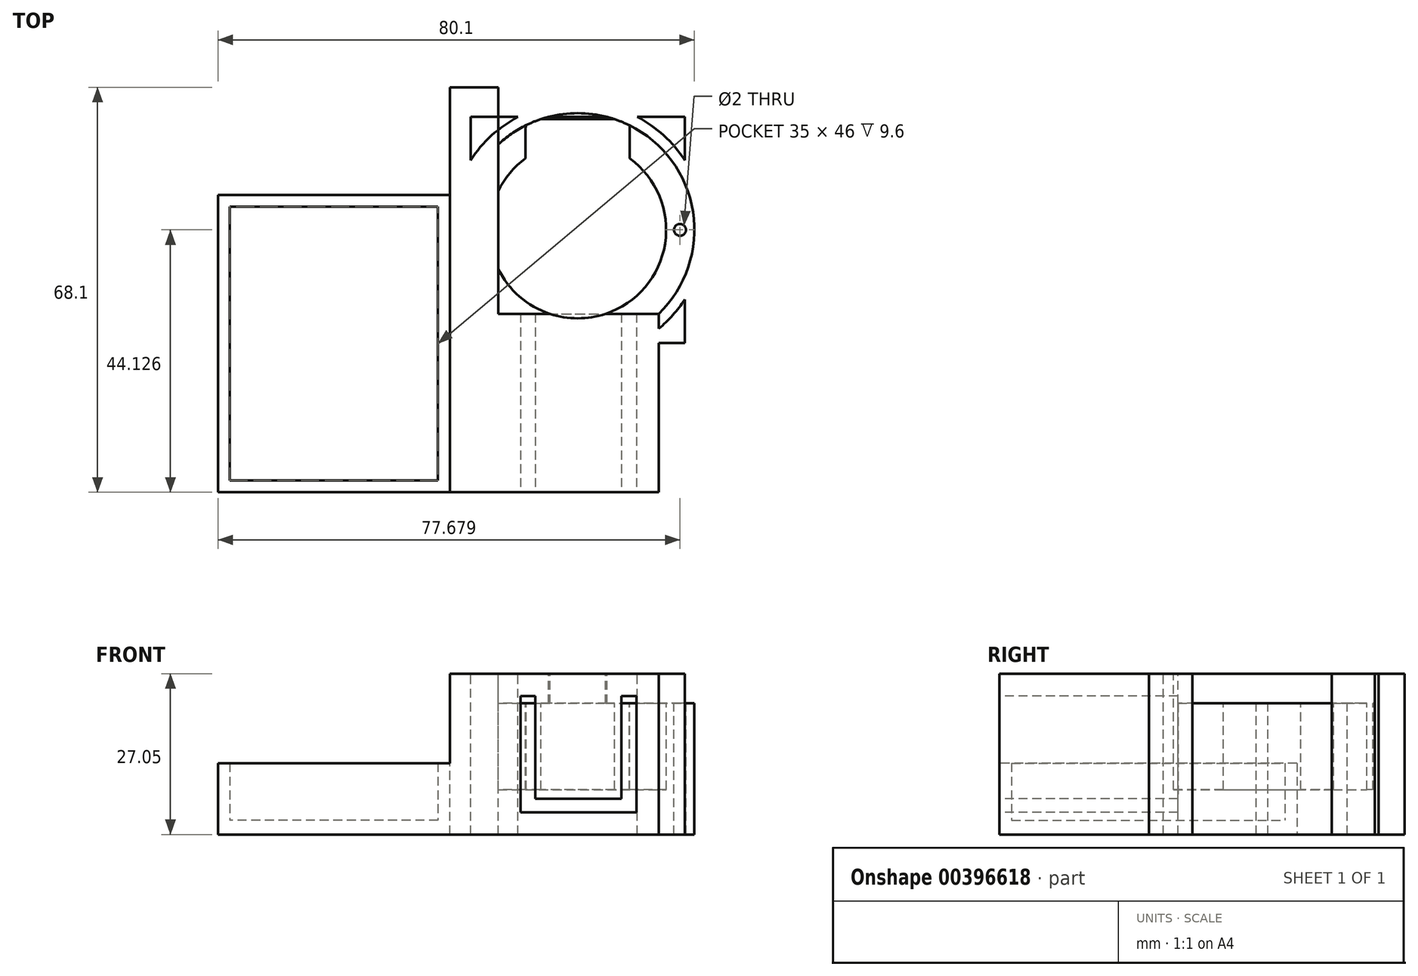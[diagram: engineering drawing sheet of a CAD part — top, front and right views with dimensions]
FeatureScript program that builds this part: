
annotation { "Feature Type Name" : "Feature", "Feature Type Description" : "" }
export const myFeature = defineFeature(function(context is Context, id is Id, definition is map)
    precondition{}
    {
        {
            var Q0;
            Q0=qCreatedBy(makeId("Front.planeOp"),FACE);
            var sketch = newSketch(context, id + "F0", { "sketchPlane" : qUnion([Q0])});
            skLineSegment(sketch, "E0", {"start": v(0, 65.65) * mm, "end": v(0, -40.44) * mm, "construction": true});
            skLineSegment(sketch, "E1", {"start": v(0, 0) * mm, "end": v(-9.75, 0) * mm});
            skLineSegment(sketch, "E2", {"start": v(-9.75, 0) * mm, "end": v(-9.75, 19.55) * mm});
            skLineSegment(sketch, "E3", {"start": v(-9.75, 19.55) * mm, "end": v(-7.25, 19.55) * mm});
            skLineSegment(sketch, "E4", {"start": v(-7.25, 19.55) * mm, "end": v(-7.25, 2.25) * mm});
            skLineSegment(sketch, "E5", {"start": v(-7.25, 2.25) * mm, "end": v(0, 2.25) * mm});
            skLineSegment(sketch, "E6.MirrorCS", {"start": v(9.75, 19.55) * mm, "end": v(7.25, 19.55) * mm});
            skLineSegment(sketch, "E7.MirrorCS", {"start": v(0, 0) * mm, "end": v(9.75, 0) * mm});
            skLineSegment(sketch, "E8.MirrorCS", {"start": v(9.75, 0) * mm, "end": v(9.75, 19.55) * mm});
            skLineSegment(sketch, "E9.MirrorCS", {"start": v(7.25, 19.55) * mm, "end": v(7.25, 2.25) * mm});
            skLineSegment(sketch, "E10.MirrorCS", {"start": v(7.25, 2.25) * mm, "end": v(0, 2.25) * mm});
            skLineSegment(sketch, "E11.0", {"start": v(-13.5, 23.3) * mm, "end": v(0, 23.3) * mm});
            skLineSegment(sketch, "E11.1", {"start": v(-13.5, -3.75) * mm, "end": v(-13.5, 23.3) * mm});
            skLineSegment(sketch, "E11.2", {"start": v(0, -3.75) * mm, "end": v(-13.5, -3.75) * mm});
            skLineSegment(sketch, "E12.MirrorCS", {"start": v(0, -3.75) * mm, "end": v(13.5, -3.75) * mm});
            skLineSegment(sketch, "E13.MirrorCS", {"start": v(13.5, 23.3) * mm, "end": v(0, 23.3) * mm});
            skLineSegment(sketch, "E14.MirrorCS", {"start": v(13.5, -3.75) * mm, "end": v(13.5, 23.3) * mm});
            skLineSegment(sketch, "E15", {"start": v(-13.5, 23.3) * mm, "end": v(-18, 23.3) * mm});
            skLineSegment(sketch, "E16", {"start": v(-18, 23.3) * mm, "end": v(-18, -3.75) * mm});
            skLineSegment(sketch, "E17", {"start": v(-18, -3.75) * mm, "end": v(-13.5, -3.75) * mm});
            skLineSegment(sketch, "E18.MirrorCS", {"start": v(18, -3.75) * mm, "end": v(13.5, -3.75) * mm});
            skLineSegment(sketch, "E19.MirrorCS", {"start": v(18, 23.3) * mm, "end": v(18, -3.75) * mm});
            skLineSegment(sketch, "E20.MirrorCS", {"start": v(13.5, 23.3) * mm, "end": v(18, 23.3) * mm});
            skSolve(sketch);
        }
        {
            var Q0;
            Q0=makeQuery(id+"F0.imprint","IMPRINT",FACE,{"disambiguationData":[TD([[makeQuery(id+"F0.imprint","IMPRINT",EDGE,{"derivedFrom":sQuery(id+"F0.wireOp",EDGE,"E1")}),1.0]])]});
            extrude(context, id + "F1", {"entities" : qUnion([Q0]), "oppositeDirection" : true, "depth" : 30 * mm});
        }
        {
            var Q0;
            {var subQ0=sQuery(id+"F0.wireOp",EDGE,"E13.MirrorCS");var subQ1=sQuery(id+"F0.wireOp",EDGE,"E11.0");Q0=makeQuery(id+"FVVeJcuvD0pZku6_1.boolean.opBoolean","MERGE",FACE,{"derivedFrom":[makeQuery(id+"F1.opExtrude","SWEPT_FACE",FACE,{"disambiguationData":[OSD([subQ1,subQ0])]}),makeQuery(id+"FVVeJcuvD0pZku6_1.opExtrude","SWEPT_FACE",FACE,{"disambiguationData":[OSD([subQ1,subQ0,sQuery(id+"F0.wireOp",EDGE,"E15"),sQuery(id+"F0.wireOp",EDGE,"E20.MirrorCS")])]})]});}
            var sketch = newSketch(context, id + "F2", { "sketchPlane" : qUnion([Q0])});
            skLineSegment(sketch, "E21.0", {"start": v(17.88, 25.13) * mm, "end": v(-0.12, 25.13) * mm});
            skLineSegment(sketch, "E21.1", {"start": v(17.88, 63.13) * mm, "end": v(17.88, 25.13) * mm});
            skLineSegment(sketch, "E21.2", {"start": v(17.88, 63.13) * mm, "end": v(-18.12, 63.13) * mm});
            skLineSegment(sketch, "E21.3", {"start": v(-18.12, 63.13) * mm, "end": v(-18.12, 25.13) * mm});
            skLineSegment(sketch, "E21.4", {"start": v(-0.12, 25.13) * mm, "end": v(-18.12, 25.13) * mm});
            skPoint(sketch, "E21.5", {"position": v(15.87, 25) * mm});
            skLineSegment(sketch, "E22", {"start": v(-0.12, 70.75) * mm, "end": v(-0.12, 19.83) * mm, "construction": true});
            skPoint(sketch, "E22.startSnap0", {"position": v(-0.12, 63.13) * mm});
            skPoint(sketch, "E23.orphan", {"position": v(-13.87, 25.13) * mm});
            skPoint(sketch, "E24.orphan", {"position": v(13.63, 25.13) * mm});
            skLineSegment(sketch, "E25", {"start": v(-27.37, 44.13) * mm, "end": v(23.52, 44.13) * mm, "construction": true});
            skPoint(sketch, "E25.startSnap0", {"position": v(-18.12, 44.13) * mm});
            skPoint(sketch, "E26", {"position": v(-0.12, 44.13) * mm});
            skCircle(sketch, "E27", {"center": v(-0.12, 44.13) * mm, "radius": 14.88 * mm});
            skCircle(sketch, "E28", {"center": v(-0.12, 44.13) * mm, "radius": 19.62 * mm});
            skPoint(sketch, "E29", {"position": v(17.08, 44.13) * mm});
            skCircle(sketch, "E30", {"center": v(17.08, 44.13) * mm, "radius": 1 * mm});
            skCircle(sketch, "E31.MirrorC", {"center": v(-17.32, 44.13) * mm, "radius": 1 * mm});
            skCircle(sketch, "E32", {"center": v(-0.12, 44.13) * mm, "radius": 21.48 * mm});
            skSolve(sketch);
        }
        {
            var Q0;
            {var subQ6=sQuery(id+"F2.wireOp",EDGE,"E28");var subQ14=sQuery(id+"F2.wireOp",EDGE,"E21.1");var subQ15=makeQuery(id+"F2.imprint","INTERSECT",VERTEX,{"disambiguationData":[OD(0.0)],"derivedFrom":[subQ14,subQ6]});Q0=makeQuery(id+"F2.imprint","IMPRINT",FACE,{"disambiguationData":[TD([[makeQuery(id+"F2.imprint","IMPRINT",EDGE,{"disambiguationData":[TD([[subQ15,-1.0]])],"derivedFrom":subQ14}),-1.0]])]});}
            var Q1;
            {var subQ0=sQuery(id+"F2.wireOp",EDGE,"E28");var subQ1=sQuery(id+"F2.wireOp",EDGE,"E21.3");var subQ2=makeQuery(id+"F2.imprint","INTERSECT",VERTEX,{"disambiguationData":[OD(0.0)],"derivedFrom":[subQ1,subQ0]});Q1=makeQuery(id+"F2.imprint","IMPRINT",FACE,{"disambiguationData":[TD([[makeQuery(id+"F2.imprint","IMPRINT",EDGE,{"disambiguationData":[TD([[subQ2,-1.0]])],"derivedFrom":subQ1}),-1.0]])]});}
            var Q2;
            {var subQ0=sQuery(id+"F2.wireOp",EDGE,"E28");var subQ1=sQuery(id+"F2.wireOp",EDGE,"E21.1");var subQ2=makeQuery(id+"F2.imprint","INTERSECT",VERTEX,{"disambiguationData":[OD(0.0)],"derivedFrom":[subQ1,subQ0]});Q2=makeQuery(id+"F2.imprint","IMPRINT",FACE,{"disambiguationData":[TD([[makeQuery(id+"F2.imprint","IMPRINT",EDGE,{"disambiguationData":[TD([[subQ2,-1.0]])],"derivedFrom":subQ1}),1.0]])]});}
            var Q3;
            {var subQ0=sQuery(id+"F2.wireOp",EDGE,"E27");var subQ1=makeQuery(id+"F1.opExtrude","CAP_EDGE",EDGE,{"disambiguationData":[OSD([sQuery(id+"F0.wireOp",EDGE,"E11.0"),sQuery(id+"F0.wireOp",EDGE,"E13.MirrorCS")])],"isStart":false});var subQ2=makeQuery(id+"F2.imprint","INTERSECT",VERTEX,{"disambiguationData":[OD(0.0)],"derivedFrom":[subQ1,subQ0]});Q3=makeQuery(id+"F2.imprint","IMPRINT",FACE,{"disambiguationData":[TD([[makeQuery(id+"F2.imprint","IMPRINT",EDGE,{"disambiguationData":[TD([[subQ2,1.0]])],"derivedFrom":subQ0}),1.0]])]});}
            var Q4;
            {var subQ0=sQuery(id+"F2.wireOp",EDGE,"E28");var subQ1=sQuery(id+"F2.wireOp",EDGE,"E21.2");var subQ2=makeQuery(id+"F2.imprint","INTERSECT",VERTEX,{"disambiguationData":[OD(0.0)],"derivedFrom":[subQ1,subQ0]});Q4=makeQuery(id+"F2.imprint","IMPRINT",FACE,{"disambiguationData":[TD([[makeQuery(id+"F2.imprint","IMPRINT",EDGE,{"disambiguationData":[TD([[subQ2,-1.0]])],"derivedFrom":subQ1}),-1.0]])]});}
            var Q5;
            {var subQ0=sQuery(id+"F2.wireOp",EDGE,"E31.MirrorC");var subQ1=sQuery(id+"F2.wireOp",EDGE,"E21.3");var subQ2=makeQuery(id+"F2.imprint","INTERSECT",VERTEX,{"disambiguationData":[OD(0.0)],"derivedFrom":[subQ1,subQ0]});Q5=makeQuery(id+"F2.imprint","IMPRINT",FACE,{"disambiguationData":[TD([[makeQuery(id+"F2.imprint","IMPRINT",EDGE,{"disambiguationData":[TD([[subQ2,-1.0]])],"derivedFrom":subQ1}),1.0]])]});}
            var Q6;
            {var subQ0=sQuery(id+"F2.wireOp",EDGE,"E31.MirrorC");var subQ1=sQuery(id+"F2.wireOp",EDGE,"E21.3");var subQ2=makeQuery(id+"F2.imprint","INTERSECT",VERTEX,{"disambiguationData":[OD(0.0)],"derivedFrom":[subQ1,subQ0]});Q6=makeQuery(id+"F2.imprint","IMPRINT",FACE,{"disambiguationData":[TD([[makeQuery(id+"F2.imprint","IMPRINT",EDGE,{"disambiguationData":[TD([[subQ2,-1.0]])],"derivedFrom":subQ1}),-1.0]])]});}
            var Q7;
            {var subQ0=sQuery(id+"F2.wireOp",EDGE,"E30");var subQ1=sQuery(id+"F2.wireOp",EDGE,"E21.1");var subQ2=makeQuery(id+"F2.imprint","INTERSECT",VERTEX,{"disambiguationData":[OD(0.0)],"derivedFrom":[subQ1,subQ0]});Q7=makeQuery(id+"F2.imprint","IMPRINT",FACE,{"disambiguationData":[TD([[makeQuery(id+"F2.imprint","IMPRINT",EDGE,{"disambiguationData":[TD([[subQ2,-1.0]])],"derivedFrom":subQ1}),-1.0]])]});}
            var Q8;
            {var subQ0=sQuery(id+"F2.wireOp",EDGE,"E30");var subQ1=sQuery(id+"F2.wireOp",EDGE,"E21.1");var subQ2=makeQuery(id+"F2.imprint","INTERSECT",VERTEX,{"disambiguationData":[OD(0.0)],"derivedFrom":[subQ1,subQ0]});Q8=makeQuery(id+"F2.imprint","IMPRINT",FACE,{"disambiguationData":[TD([[makeQuery(id+"F2.imprint","IMPRINT",EDGE,{"disambiguationData":[TD([[subQ2,-1.0]])],"derivedFrom":subQ1}),1.0]])]});}
            var Q9;
            {var subQ0=sQuery(id+"F2.wireOp",EDGE,"E32");var subQ1=sQuery(id+"F2.wireOp",EDGE,"E21.3");var subQ2=makeQuery(id+"F2.imprint","INTERSECT",VERTEX,{"disambiguationData":[OD(0.0)],"derivedFrom":[subQ1,subQ0]});Q9=makeQuery(id+"F2.imprint","IMPRINT",FACE,{"disambiguationData":[TD([[makeQuery(id+"F2.imprint","IMPRINT",EDGE,{"disambiguationData":[TD([[subQ2,-1.0]])],"derivedFrom":subQ1}),-1.0]])]});}
            var Q10;
            {var subQ0=sQuery(id+"F2.wireOp",EDGE,"E32");var subQ1=sQuery(id+"F2.wireOp",EDGE,"E21.2");var subQ2=makeQuery(id+"F2.imprint","INTERSECT",VERTEX,{"disambiguationData":[OD(1.0)],"derivedFrom":[subQ1,subQ0]});Q10=makeQuery(id+"F2.imprint","IMPRINT",FACE,{"disambiguationData":[TD([[makeQuery(id+"F2.imprint","IMPRINT",EDGE,{"disambiguationData":[TD([[subQ2,1.0]])],"derivedFrom":subQ1}),1.0]])]});}
            var Q11;
            {var subQ0=sQuery(id+"F2.wireOp",EDGE,"E32");var subQ1=sQuery(id+"F2.wireOp",EDGE,"E21.1");var subQ2=makeQuery(id+"F2.imprint","INTERSECT",VERTEX,{"disambiguationData":[OD(0.0)],"derivedFrom":[subQ1,subQ0]});Q11=makeQuery(id+"F2.imprint","IMPRINT",FACE,{"disambiguationData":[TD([[makeQuery(id+"F2.imprint","IMPRINT",EDGE,{"disambiguationData":[TD([[subQ2,-1.0]])],"derivedFrom":subQ1}),-1.0]])]});}
            var Q12;
            {var subQ0=sQuery(id+"F2.wireOp",EDGE,"E32");var subQ1=sQuery(id+"F2.wireOp",EDGE,"E21.2");var subQ2=makeQuery(id+"F2.imprint","INTERSECT",VERTEX,{"disambiguationData":[OD(0.0)],"derivedFrom":[subQ1,subQ0]});Q12=makeQuery(id+"F2.imprint","IMPRINT",FACE,{"disambiguationData":[TD([[makeQuery(id+"F2.imprint","IMPRINT",EDGE,{"disambiguationData":[TD([[subQ2,-1.0]])],"derivedFrom":subQ1}),-1.0]])]});}
            var Q13;
            {var subQ0=sQuery(id+"F2.wireOp",EDGE,"E32");var subQ1=sQuery(id+"F2.wireOp",EDGE,"E21.1");var subQ2=makeQuery(id+"F2.imprint","INTERSECT",VERTEX,{"disambiguationData":[OD(0.0)],"derivedFrom":[subQ1,subQ0]});Q13=makeQuery(id+"F2.imprint","IMPRINT",FACE,{"disambiguationData":[TD([[makeQuery(id+"F2.imprint","IMPRINT",EDGE,{"disambiguationData":[TD([[subQ2,-1.0]])],"derivedFrom":subQ1}),1.0]])]});}
            var Q14;
            {var subQ0=sQuery(id+"F2.wireOp",EDGE,"E32");var subQ1=sQuery(id+"F2.wireOp",EDGE,"E21.1");var subQ2=makeQuery(id+"F2.imprint","INTERSECT",VERTEX,{"disambiguationData":[OD(1.0)],"derivedFrom":[subQ1,subQ0]});Q14=makeQuery(id+"F2.imprint","IMPRINT",FACE,{"disambiguationData":[TD([[makeQuery(id+"F2.imprint","IMPRINT",EDGE,{"disambiguationData":[TD([[subQ2,1.0]])],"derivedFrom":subQ1}),-1.0]])]});}
            var Q15;
            {var subQ0=sQuery(id+"F2.wireOp",EDGE,"E32");var subQ1=sQuery(id+"F2.wireOp",EDGE,"E21.3");var subQ2=makeQuery(id+"F2.imprint","INTERSECT",VERTEX,{"disambiguationData":[OD(1.0)],"derivedFrom":[subQ1,subQ0]});Q15=makeQuery(id+"F2.imprint","IMPRINT",FACE,{"disambiguationData":[TD([[makeQuery(id+"F2.imprint","IMPRINT",EDGE,{"disambiguationData":[TD([[subQ2,1.0]])],"derivedFrom":subQ1}),1.0]])]});}
            var Q16;
            Q16=makeQuery(id+"F1.opExtrude","SWEPT_FACE",FACE,{"disambiguationData":[OSD([sQuery(id+"F0.wireOp",EDGE,"E11.2"),sQuery(id+"F0.wireOp",EDGE,"E12.MirrorCS")])]});
            extrude(context, id + "F3", {"entities" : qUnion([Q0, Q1, Q2, Q3, Q4, Q5, Q6, Q7, Q8, Q9, Q10, Q11, Q12, Q13, Q14, Q15]), "operationType" : NewBodyOperationType.ADD, "endBound" : BoundingType.UP_TO_SURFACE, "oppositeDirection" : true, "endBoundEntityFace" : qUnion([Q16]), "depth" : 25 * mm});
        }
        {
            var Q0;
            {var subQ0=sQuery(id+"F2.wireOp",EDGE,"E27");var subQ1=makeQuery(id+"F1.opExtrude","CAP_EDGE",EDGE,{"disambiguationData":[OSD([sQuery(id+"F0.wireOp",EDGE,"E11.0"),sQuery(id+"F0.wireOp",EDGE,"E13.MirrorCS")])],"isStart":false});var subQ2=makeQuery(id+"F2.imprint","INTERSECT",VERTEX,{"disambiguationData":[OD(0.0)],"derivedFrom":[subQ1,subQ0]});Q0=makeQuery(id+"F2.imprint","IMPRINT",FACE,{"disambiguationData":[TD([[makeQuery(id+"F2.imprint","IMPRINT",EDGE,{"disambiguationData":[TD([[subQ2,1.0]])],"derivedFrom":subQ0}),1.0]])]});}
            var Q1;
            {var subQ0=sQuery(id+"F2.wireOp",EDGE,"E27");var subQ1=makeQuery(id+"F1.opExtrude","CAP_EDGE",EDGE,{"disambiguationData":[OSD([sQuery(id+"F0.wireOp",EDGE,"E11.0"),sQuery(id+"F0.wireOp",EDGE,"E13.MirrorCS")])],"isStart":false});var subQ2=makeQuery(id+"F2.imprint","INTERSECT",VERTEX,{"disambiguationData":[OD(0.0)],"derivedFrom":[subQ1,subQ0]});Q1=makeQuery(id+"F2.imprint","IMPRINT",FACE,{"disambiguationData":[TD([[makeQuery(id+"F2.imprint","IMPRINT",EDGE,{"disambiguationData":[TD([[subQ2,-1.0]])],"derivedFrom":subQ0}),1.0]])]});}
            extrude(context, id + "F4", {"entities" : qUnion([Q0, Q1]), "operationType" : NewBodyOperationType.REMOVE, "oppositeDirection" : true, "depth" : 19.5 * mm});
        }
        {
            var Q0;
            {var subQ0=sQuery(id+"F2.wireOp",EDGE,"E31.MirrorC");var subQ1=sQuery(id+"F2.wireOp",EDGE,"E21.3");var subQ2=makeQuery(id+"F2.imprint","INTERSECT",VERTEX,{"disambiguationData":[OD(0.0)],"derivedFrom":[subQ1,subQ0]});Q0=makeQuery(id+"F2.imprint","IMPRINT",FACE,{"disambiguationData":[TD([[makeQuery(id+"F2.imprint","IMPRINT",EDGE,{"disambiguationData":[TD([[subQ2,-1.0]])],"derivedFrom":subQ1}),1.0]])]});}
            var Q1;
            {var subQ0=sQuery(id+"F2.wireOp",EDGE,"E31.MirrorC");var subQ1=sQuery(id+"F2.wireOp",EDGE,"E21.3");var subQ2=makeQuery(id+"F2.imprint","INTERSECT",VERTEX,{"disambiguationData":[OD(0.0)],"derivedFrom":[subQ1,subQ0]});Q1=makeQuery(id+"F2.imprint","IMPRINT",FACE,{"disambiguationData":[TD([[makeQuery(id+"F2.imprint","IMPRINT",EDGE,{"disambiguationData":[TD([[subQ2,-1.0]])],"derivedFrom":subQ1}),-1.0]])]});}
            var Q2;
            {var subQ0=sQuery(id+"F2.wireOp",EDGE,"E30");var subQ1=sQuery(id+"F2.wireOp",EDGE,"E21.1");var subQ2=makeQuery(id+"F2.imprint","INTERSECT",VERTEX,{"disambiguationData":[OD(0.0)],"derivedFrom":[subQ1,subQ0]});Q2=makeQuery(id+"F2.imprint","IMPRINT",FACE,{"disambiguationData":[TD([[makeQuery(id+"F2.imprint","IMPRINT",EDGE,{"disambiguationData":[TD([[subQ2,-1.0]])],"derivedFrom":subQ1}),-1.0]])]});}
            var Q3;
            {var subQ0=sQuery(id+"F2.wireOp",EDGE,"E30");var subQ1=sQuery(id+"F2.wireOp",EDGE,"E21.1");var subQ2=makeQuery(id+"F2.imprint","INTERSECT",VERTEX,{"disambiguationData":[OD(0.0)],"derivedFrom":[subQ1,subQ0]});Q3=makeQuery(id+"F2.imprint","IMPRINT",FACE,{"disambiguationData":[TD([[makeQuery(id+"F2.imprint","IMPRINT",EDGE,{"disambiguationData":[TD([[subQ2,-1.0]])],"derivedFrom":subQ1}),1.0]])]});}
            var Q4;
            Q4=sQuery(id+"F2.wireOp",EDGE,"E31.MirrorC");
            var Q5;
            Q5=sQuery(id+"F2.wireOp",EDGE,"E30");
            extrude(context, id + "F5", {"entities" : qUnion([Q0, Q1, Q2, Q3]), "operationType" : NewBodyOperationType.REMOVE, "surfaceEntities" : qUnion([Q4, Q5]), "oppositeDirection" : true, "depth" : 5 * mm});
        }
        {
            var Q0;
            {var subQ0=sQuery(id+"F0.wireOp",EDGE,"E13.MirrorCS");var subQ1=sQuery(id+"F0.wireOp",EDGE,"E11.0");Q0=makeQuery(id+"F3.boolean.opBoolean","MERGE",FACE,{"derivedFrom":[makeQuery(id+"F1.opExtrude","SWEPT_FACE",FACE,{"disambiguationData":[OSD([subQ1,subQ0])]}),makeQuery(id+"F3.opExtrude","CAP_FACE",FACE,{"disambiguationData":[OSD([subQ1,sQuery(id+"F0.wireOp",EDGE,"E11.1"),subQ0,sQuery(id+"F0.wireOp",EDGE,"E14.MirrorCS"),sQuery(id+"F0.wireOp",EDGE,"E15"),sQuery(id+"F0.wireOp",EDGE,"E20.MirrorCS"),sQuery(id+"F2.wireOp",EDGE,"E32")])],"isStart":true})]});}
            var sketch = newSketch(context, id + "F6", { "sketchPlane" : qUnion([Q0])});
            skArc(sketch, "E33.0", {"start": v(13.5, 27.51) * mm, "mid": v(-0.28, 65.6) * mm, "end": v(-13.5, 27.32) * mm});
            skLineSegment(sketch, "E34", {"start": v(-0.12, 29.25) * mm, "end": v(-0.12, 72.13) * mm, "construction": true});
            skPoint(sketch, "E35", {"position": v(-0.12, 62.75) * mm});
            skLineSegment(sketch, "E36", {"start": v(-0.12, 62.75) * mm, "end": v(-7.37, 62.75) * mm});
            skLineSegment(sketch, "E37", {"start": v(-8.87, 61.25) * mm, "end": v(-8.87, 56.15) * mm});
            skPoint(sketch, "E38.visualSharp", {"position": v(-8.87, 62.75) * mm});
            skArc(sketch, "E38.filletArc", {"start": v(-7.37, 62.75) * mm, "mid": v(-8.43, 62.31) * mm, "end": v(-8.87, 61.25) * mm});
            skArc(sketch, "E39", {"start": v(-8.87, 56.15) * mm, "mid": v(4.48, 29.98) * mm, "end": v(-0.12, 59) * mm});
            skArc(sketch, "E40", {"start": v(-0.12, 59) * mm, "mid": v(-4.72, 58.27) * mm, "end": v(-8.87, 56.15) * mm});
            skArc(sketch, "E41.MirrorCS", {"start": v(-0.12, 59) * mm, "mid": v(4.48, 58.27) * mm, "end": v(8.63, 56.15) * mm});
            skLineSegment(sketch, "E42.MirrorCS", {"start": v(-0.12, 62.75) * mm, "end": v(7.13, 62.75) * mm});
            skLineSegment(sketch, "E43.MirrorCS", {"start": v(8.63, 61.25) * mm, "end": v(8.63, 56.15) * mm});
            skArc(sketch, "E44.MirrorCS", {"start": v(7.13, 62.75) * mm, "mid": v(8.19, 62.31) * mm, "end": v(8.63, 61.25) * mm});
            skSolve(sketch);
        }
        {
            var Q0;
            Q0=makeQuery(id+"F6.imprint","IMPRINT",FACE,{"disambiguationData":[TD([[makeQuery(id+"F6.imprint","IMPRINT",EDGE,{"derivedFrom":sQuery(id+"F6.wireOp",EDGE,"E36")}),1.0]])]});
            var Q1;
            Q1=makeQuery(id+"F4.boolean.opBoolean","COPY",FACE,{"derivedFrom":makeQuery(id+"F4.opExtrude","CAP_FACE",FACE,{"disambiguationData":[OSD([sQuery(id+"F2.wireOp",EDGE,"E27")])],"isStart":false})});
            extrude(context, id + "F7", {"entities" : qUnion([Q0]), "operationType" : NewBodyOperationType.REMOVE, "endBound" : BoundingType.UP_TO_SURFACE, "oppositeDirection" : true, "endBoundEntityFace" : qUnion([Q1]), "depth" : 25 * mm});
        }
        {
            var Q0;
            Q0=makeQuery(id+"F1.opExtrude","CAP_FACE",FACE,{"disambiguationData":[OSD([sQuery(id+"F0.wireOp",EDGE,"E1"),sQuery(id+"F0.wireOp",EDGE,"E2"),sQuery(id+"F0.wireOp",EDGE,"E3"),sQuery(id+"F0.wireOp",EDGE,"E4"),sQuery(id+"F0.wireOp",EDGE,"E5"),sQuery(id+"F0.wireOp",EDGE,"E6.MirrorCS"),sQuery(id+"F0.wireOp",EDGE,"E7.MirrorCS"),sQuery(id+"F0.wireOp",EDGE,"E8.MirrorCS"),sQuery(id+"F0.wireOp",EDGE,"E9.MirrorCS"),sQuery(id+"F0.wireOp",EDGE,"E10.MirrorCS"),sQuery(id+"F0.wireOp",EDGE,"E11.0"),sQuery(id+"F0.wireOp",EDGE,"E11.1"),sQuery(id+"F0.wireOp",EDGE,"E11.2"),sQuery(id+"F0.wireOp",EDGE,"E12.MirrorCS"),sQuery(id+"F0.wireOp",EDGE,"E13.MirrorCS"),sQuery(id+"F0.wireOp",EDGE,"E14.MirrorCS")])],"isStart":true});
            var sketch = newSketch(context, id + "F8", { "sketchPlane" : qUnion([Q0])});
            skPoint(sketch, "E45.0", {"position": v(-13.5, 23.3) * mm});
            skPoint(sketch, "E45.1", {"position": v(-13.5, -3.75) * mm});
            skLineSegment(sketch, "E45.2.0", {"start": v(13.5, 23.3) * mm, "end": v(13.5, -3.75) * mm});
            skLineSegment(sketch, "E45.2.1", {"start": v(-21.6, -3.75) * mm, "end": v(21.36, -3.75) * mm});
            skLineSegment(sketch, "E45.2.2", {"start": v(-13.5, -3.75) * mm, "end": v(-13.5, 23.3) * mm});
            skLineSegment(sketch, "E45.2.3", {"start": v(21.36, 23.3) * mm, "end": v(-21.6, 23.3) * mm});
            skLineSegment(sketch, "E46", {"start": v(-21.6, 23.3) * mm, "end": v(-21.6, -3.75) * mm});
            skSolve(sketch);
        }
        {
            var Q0;
            {var subQ0=sQuery(id+"F8.wireOp",EDGE,"E45.2.2");Q0=makeQuery(id+"F8.imprint","IMPRINT",FACE,{"disambiguationData":[TD([[makeQuery(id+"F8.imprint","IMPRINT",EDGE,{"derivedFrom":subQ0}),1.0]])]});}
            extrude(context, id + "F9", {"entities" : qUnion([Q0]), "oppositeDirection" : true, "depth" : 68.1 * mm, "offsetDistance" : 25 * mm});
        }
        {
            var Q0;
            Q0=makeQuery(id+"F9.opExtrude","SWEPT_FACE",FACE,{"disambiguationData":[OSD([sQuery(id+"F8.wireOp",EDGE,"E46")])]});
            var sketch = newSketch(context, id + "F10", { "sketchPlane" : qUnion([Q0])});
            skLineSegment(sketch, "E47.0.0", {"start": v(-27.51, 23.3) * mm, "end": v(-27.51, -3.75) * mm});
            skLineSegment(sketch, "E47.0.1", {"start": v(-65.6, -3.75) * mm, "end": v(-27.32, -3.75) * mm});
            skLineSegment(sketch, "E47.0.2", {"start": v(-27.32, -3.75) * mm, "end": v(-27.32, 23.3) * mm});
            skLineSegment(sketch, "E47.0.3", {"start": v(-27.32, 23.3) * mm, "end": v(-65.6, 23.3) * mm});
            skLineSegment(sketch, "E47.1.0", {"start": v(-27.32, 23.3) * mm, "end": v(-27.32, -3.75) * mm});
            skLineSegment(sketch, "E47.1.1", {"start": v(-27.32, -3.75) * mm, "end": v(0, -3.75) * mm});
            skLineSegment(sketch, "E47.1.2", {"start": v(0, -3.75) * mm, "end": v(0, 23.3) * mm});
            skLineSegment(sketch, "E47.1.3", {"start": v(0, 23.3) * mm, "end": v(-27.32, 23.3) * mm});
            skLineSegment(sketch, "E48", {"start": v(-65.6, 23.3) * mm, "end": v(-65.6, -3.75) * mm});
            skPoint(sketch, "E49", {"position": v(-65.6, 8.25) * mm});
            skLineSegment(sketch, "E50", {"start": v(-65.6, 8.25) * mm, "end": v(0, 8.25) * mm});
            skSolve(sketch);
        }
        {
            var Q0;
            {var subQ0=sQuery(id+"F0.wireOp",EDGE,"E12.MirrorCS");var subQ1=sQuery(id+"F0.wireOp",EDGE,"E11.2");Q0=makeQuery(id+"F3.boolean.opBoolean","MERGE",FACE,{"derivedFrom":[makeQuery(id+"F1.opExtrude","SWEPT_FACE",FACE,{"disambiguationData":[OSD([subQ1,subQ0])]}),makeQuery(id+"F3.opExtrude","CAP_FACE",FACE,{"disambiguationData":[OSD([subQ1,subQ0])],"isStart":false})]});}
            var sketch = newSketch(context, id + "F11", { "sketchPlane" : qUnion([Q0])});
            skLineSegment(sketch, "E51.0", {"start": v(-13.5, -27.32) * mm, "end": v(-13.5, 0) * mm});
            skArc(sketch, "E51.1", {"start": v(13.5, -27.51) * mm, "mid": v(-0.28, -65.6) * mm, "end": v(-13.5, -27.32) * mm});
            skLineSegment(sketch, "E51.2", {"start": v(-21.6, -50) * mm, "end": v(-21.6, 0) * mm});
            skLineSegment(sketch, "E51.3", {"start": v(13.5, -27.51) * mm, "end": v(13.5, 0) * mm});
            skLineSegment(sketch, "E51.4", {"start": v(-13.5, 0) * mm, "end": v(13.5, 0) * mm});
            skLineSegment(sketch, "E52", {"start": v(-21.6, 0) * mm, "end": v(-60.6, 0) * mm});
            skLineSegment(sketch, "E53", {"start": v(-60.6, 0) * mm, "end": v(-60.6, -50) * mm});
            skLineSegment(sketch, "E54", {"start": v(-21.6, -50) * mm, "end": v(-60.6, -50) * mm});
            skLineSegment(sketch, "E55", {"start": v(-21.6, 0) * mm, "end": v(-13.5, 0) * mm});
            skPoint(sketch, "E56.orphan", {"position": v(-21.6, -65.6) * mm});
            skLineSegment(sketch, "E57", {"start": v(-21.6, -50) * mm, "end": v(-20.79, -50) * mm});
            skLineSegment(sketch, "E58.0", {"start": v(-23.6, -2) * mm, "end": v(-58.6, -2) * mm});
            skLineSegment(sketch, "E58.1", {"start": v(-23.6, -48) * mm, "end": v(-23.6, -2) * mm});
            skLineSegment(sketch, "E58.2", {"start": v(-23.6, -48) * mm, "end": v(-58.6, -48) * mm});
            skLineSegment(sketch, "E58.3", {"start": v(-58.6, -2) * mm, "end": v(-58.6, -48) * mm});
            skSolve(sketch);
        }
        {
            var Q0;
            {var subQ0=sQuery(id+"F11.wireOp",EDGE,"E52");Q0=makeQuery(id+"F11.imprint","IMPRINT",FACE,{"disambiguationData":[TD([[makeQuery(id+"F11.imprint","IMPRINT",EDGE,{"derivedFrom":subQ0}),1.0]])]});}
            var Q1;
            {var subQ0=sQuery(id+"F11.wireOp",EDGE,"E51.0");Q1=makeQuery(id+"F11.imprint","IMPRINT",FACE,{"disambiguationData":[TD([[makeQuery(id+"F11.imprint","IMPRINT",EDGE,{"derivedFrom":subQ0}),1.0]])]});}
            var Q2;
            {var subQ3=sQuery(id+"F11.wireOp",EDGE,"E57");Q2=makeQuery(id+"F11.imprint","IMPRINT",FACE,{"disambiguationData":[TD([[makeQuery(id+"F11.imprint","IMPRINT",EDGE,{"derivedFrom":subQ3}),1.0]])]});}
            extrude(context, id + "F12", {"entities" : qUnion([Q0, Q1, Q2]), "operationType" : NewBodyOperationType.ADD, "oppositeDirection" : true, "depth" : 12 * mm, "offsetDistance" : 25 * mm});
        }
        {
            var Q0;
            Q0=makeQuery(id+"F11.imprint","IMPRINT",FACE,{"disambiguationData":[TD([[makeQuery(id+"F11.imprint","IMPRINT",EDGE,{"derivedFrom":sQuery(id+"F11.wireOp",EDGE,"E58.0")}),1.0]])]});
            extrude(context, id + "F13", {"entities" : qUnion([Q0]), "operationType" : NewBodyOperationType.ADD, "oppositeDirection" : true, "depth" : (12 - 9.6) * mm, "offsetDistance" : 25 * mm});
        }
    });
